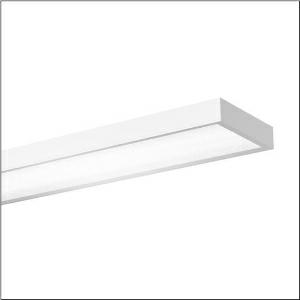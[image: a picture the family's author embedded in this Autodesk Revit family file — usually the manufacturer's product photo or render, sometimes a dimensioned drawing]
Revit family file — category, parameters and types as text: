
# Revit family: sport_31_51hs12dd4jca
name_source: partatom
category: Lighting Fixtures
units: mm (PartAtom-declared; Revit-internal decimal feet)

## family parameters
Cut with Voids When Loaded = No
Host = Face
Light Source = No
Part Type = Normal
Room Calculation Point = No
Round Connector Dimension = Use Diameter
Shared = No

## types (1)
- --- (1 x LED, 19720 lm, 146.2 W, 4000K)
    Apparent Load = 146 VA
    CIE Flux Codes = 65 89 97 100 100
    Color Rendering = 80
    Color Temperature = 4000K
    Default Elevation = 1800 mm
    Description = Sport 31, LED high bay luminaire, primary light control with reflector, of sheet steel, primary anti-glare with prismatic structure, of PC, primary optical cover: cover panel, of PC, light emission: direct distribution, primary light characteristic: symmetric, installation type: suspended mounting, recessed, surface-mounted, LED, rated luminous flux: 20.000lm, luminous efficacy: 137lm/W, light colour: 840, colour temperature: 4000K, control gear: ECG DALI, with terminal, 5-pole, max. 2.5mm², mains connection: 220..240V, AC, 50/60Hz, rated input power: 146W, housing, of sheet steel, traffic white (RAL 9016), length: 1.540mm, width: 415mm, height: 95mm, protection rating (complete): IP20, protection rating (lamp compartment, on room side): IP50, insulation class (complete): insulation class I (protective earthing), certification: CE, ENEC, UKCA, ball protection: ball impact resistant with ceiling mounting or chain suspension, impact resistance: IK08, permissible operating ambient temperature: -20..+35°C, standard: DIN 18032-3, packaging unit: 1 piece
    Height = 100 mm  [stored 0.328084 ft]
    Lamp = 1 x LED
    Lamp Light Flux = 19720 lm
    Lamp Power = 146.2 W
    Lamp count = 1
    Length = 1500 mm
    Luminous efficacy = 135 lm/W
    Manufacturer = Siteco
    ModVariant = No
    Model = 51HS12DD4JCA
    Mounting Place = Ceiling
    Mounting Type = Pendant
    Number of Poles = 1
    OnlyDefault = Yes
    Power Factor = 1
    Product Name = Sport 31
    Product group = LED high bay luminaire
    ProductGroupID = 903
    Protection Class = Protection class I
    Protection Degree = IP 20
    RLX_Detail_Level = 1
    RlxData = <blob elided: 24113 chars, md5=fc20252f>
    Socket = socket
    Standby Power = 0 W
    System Light Flux = 19719 lm
    System Power = 146 W
    Type Comments = factory setting: luminous flux: 100 % | dim-lin: 254 | 610 mA
    Type Image = l_1006829.jpg
    URL = http://relux.com
    VarID = @adj_121021
    Voltage = 0 V
    Weight = 0.00 kg
    Width = 415 mm

note: [stored X ft] marks values corroborated as IEEE doubles in the binary element streams (Revit-internal decimal feet)

## geometry (parser evidence)
native form markers: Blend x4, Sweep x10
no freeform markers — native parametric forms only
